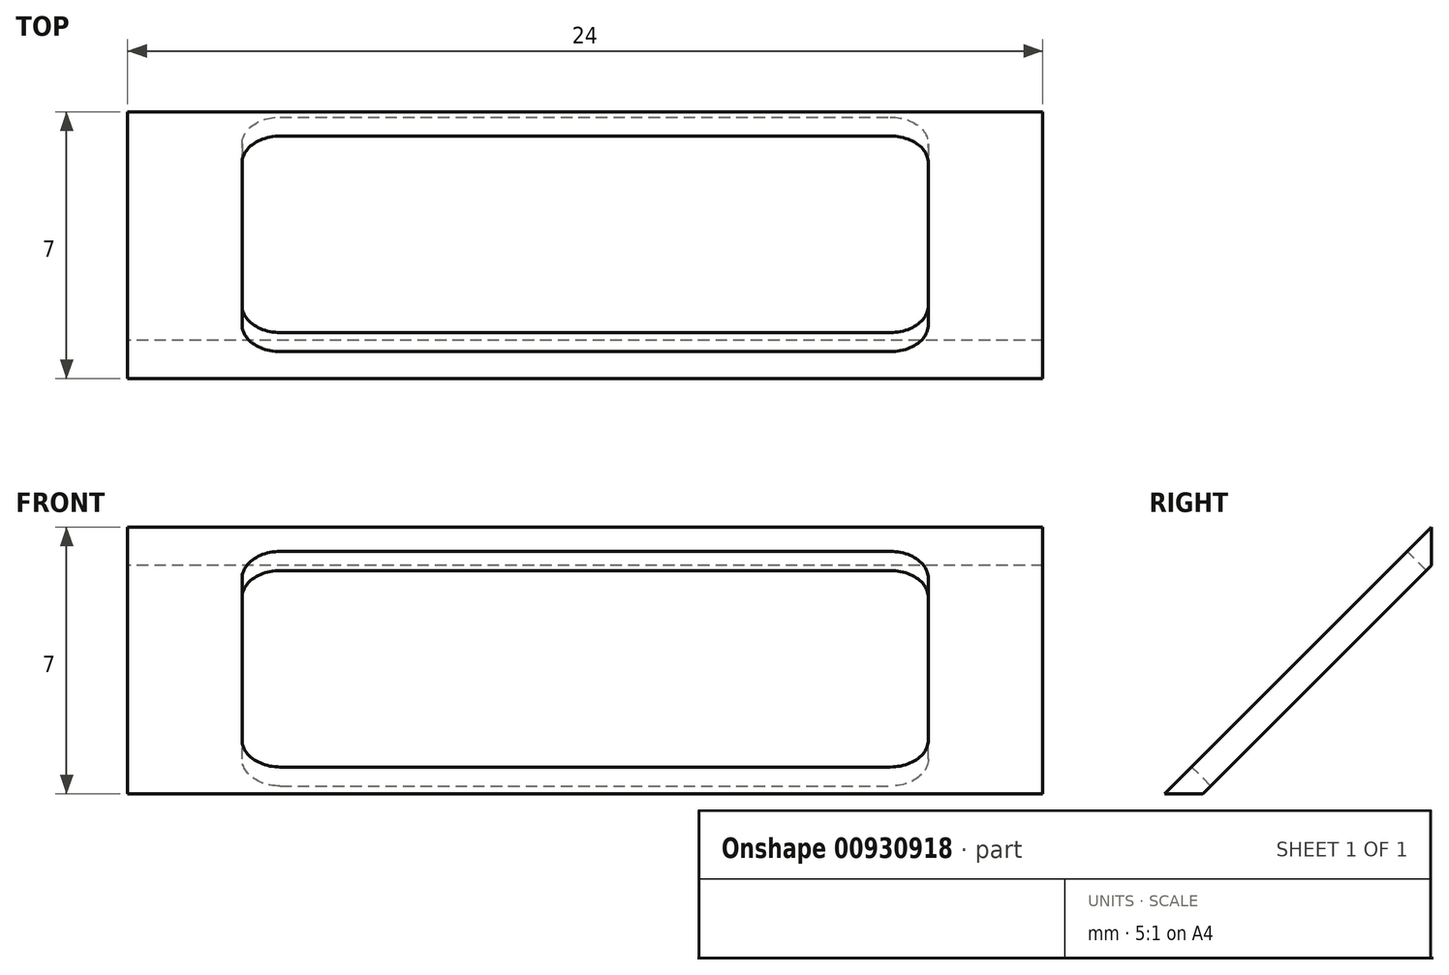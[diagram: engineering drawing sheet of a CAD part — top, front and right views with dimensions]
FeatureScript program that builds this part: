
annotation { "Feature Type Name" : "Feature", "Feature Type Description" : "" }
export const myFeature = defineFeature(function(context is Context, id is Id, definition is map)
    precondition{}
    {
        {
            var Q0;
            Q0=qCreatedBy(makeId("Right.planeOp"),FACE);
            var sketch = newSketch(context, id + "F0", { "sketchPlane" : qUnion([Q0])});
            skPoint(sketch, "E0.middle", {"position": v(0, 0) * mm});
            skLineSegment(sketch, "E1", {"start": v(-0.5, 7.5) * mm, "end": v(-6.5, 1.5) * mm});
            skPoint(sketch, "E2.orphan", {"position": v(-6.5, 7.5) * mm});
            skLineSegment(sketch, "E3", {"start": v(-0.5, 7.5) * mm, "end": v(-0.5, 8.5) * mm});
            skLineSegment(sketch, "E4", {"start": v(-6.5, 1.5) * mm, "end": v(-7.5, 1.5) * mm});
            skLineSegment(sketch, "E5", {"start": v(-7.5, 1.5) * mm, "end": v(-0.5, 8.5) * mm});
            skPoint(sketch, "E0.bottom.start.orphan", {"position": v(6.5, 7.5) * mm});
            skPoint(sketch, "E0.top.end.orphan", {"position": v(-6.5, -7.5) * mm});
            skPoint(sketch, "E0.top.start.orphan", {"position": v(6.5, -7.5) * mm});
            skSolve(sketch);
        }
        {
            var Q0;
            Q0=makeQuery(id+"F0.imprint","IMPRINT",FACE,{"disambiguationData":[TD([[makeQuery(id+"F0.imprint","IMPRINT",EDGE,{"derivedFrom":sQuery(id+"F0.wireOp",EDGE,"E1")}),-1.0]])]});
            extrude(context, id + "F1", {"entities" : qUnion([Q0]), "depth" : 24 * mm, "offsetDistance" : 25 * mm});
        }
        {
            var Q0;
            Q0=makeQuery(id+"F1.opExtrude","SWEPT_FACE",FACE,{"disambiguationData":[OSD([sQuery(id+"F0.wireOp",EDGE,"E5")])]});
            var sketch = newSketch(context, id + "F2", { "sketchPlane" : qUnion([Q0])});
            skSolve(sketch);
        }
        {
            var Q0;
            {var subQ0=sQuery(id+"F0.wireOp",EDGE,"E5");Q0=makeQuery(id+"F2.imprint","IMPRINT",FACE,{"disambiguationData":[TD([[makeQuery(id+"F2.imprint","IMPRINT",EDGE,{"derivedFrom":makeQuery(id+"F1.opExtrude","CAP_EDGE",EDGE,{"disambiguationData":[OSD([subQ0])],"isStart":true})}),-1.0]])]});}
            cPlane(context, id + "F3", {"entities" : qUnion([Q0]), "cplaneType" : CPlaneType.OFFSET, "offset" : 0 * mm, "width" : 150 * mm, "height" : 150 * mm});
        }
        {
            var Q0;
            Q0=qCreatedBy(id+"F3.planeOp",FACE);
            var sketch = newSketch(context, id + "F4", { "sketchPlane" : qUnion([Q0])});
            skLineSegment(sketch, "E6.bottom", {"start": v(20, 4.76) * mm, "end": v(4, 4.76) * mm});
            skLineSegment(sketch, "E6.top", {"start": v(20, -3.24) * mm, "end": v(4, -3.24) * mm});
            skLineSegment(sketch, "E6.left", {"start": v(21, 3.76) * mm, "end": v(21, -2.24) * mm});
            skLineSegment(sketch, "E6.right", {"start": v(3, 3.76) * mm, "end": v(3, -2.24) * mm});
            skPoint(sketch, "E6.middle", {"position": v(12, 0.76) * mm});
            skPoint(sketch, "E7.visualSharp", {"position": v(21, 4.76) * mm});
            skArc(sketch, "E7.filletArc", {"start": v(21, 3.76) * mm, "mid": v(20.7, 4.46) * mm, "end": v(20, 4.76) * mm});
            skPoint(sketch, "E8.visualSharp", {"position": v(21, -3.24) * mm});
            skArc(sketch, "E8.filletArc", {"start": v(20, -3.24) * mm, "mid": v(20.7, -2.95) * mm, "end": v(21, -2.24) * mm});
            skPoint(sketch, "E9.visualSharp", {"position": v(3, -3.24) * mm});
            skArc(sketch, "E9.filletArc", {"start": v(3, -2.24) * mm, "mid": v(3.3, -2.95) * mm, "end": v(4, -3.24) * mm});
            skPoint(sketch, "E10.visualSharp", {"position": v(3, 4.76) * mm});
            skArc(sketch, "E10.filletArc", {"start": v(4, 4.76) * mm, "mid": v(3.3, 4.46) * mm, "end": v(3, 3.76) * mm});
            skSolve(sketch);
        }
        {
            var Q0;
            Q0 = qSketchRegion(id + "F4", true);
            extrude(context, id + "F5", {"entities" : qUnion([Q0]), "operationType" : NewBodyOperationType.REMOVE, "oppositeDirection" : true, "depth" : 25 * mm, "offsetDistance" : 25 * mm});
        }
    });
